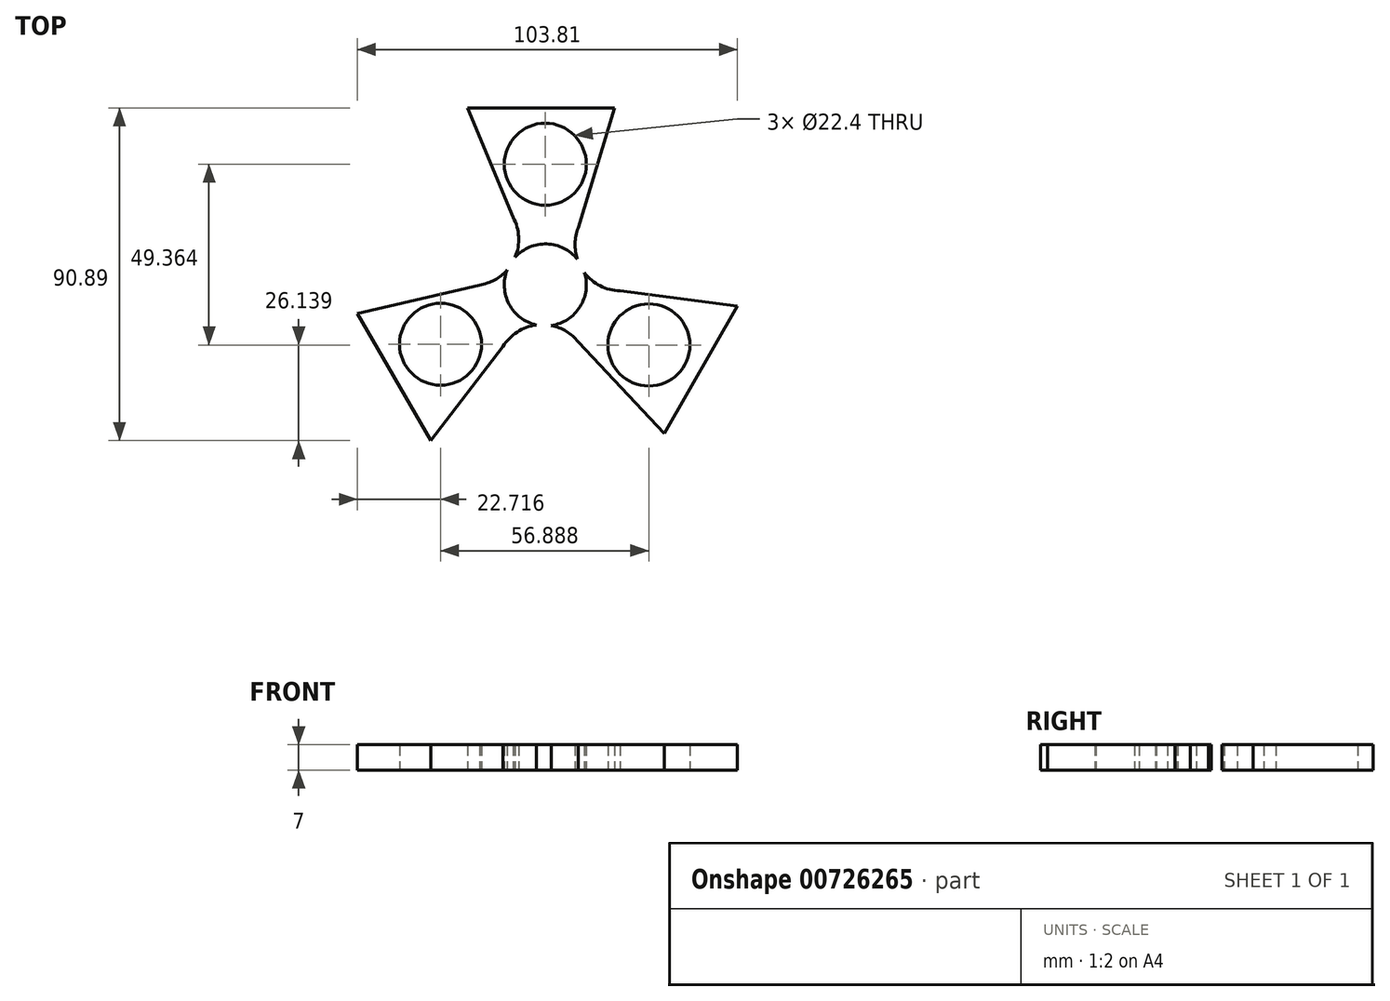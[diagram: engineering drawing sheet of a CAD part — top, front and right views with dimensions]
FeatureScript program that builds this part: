
annotation { "Feature Type Name" : "Feature", "Feature Type Description" : "" }
export const myFeature = defineFeature(function(context is Context, id is Id, definition is map)
    precondition{}
    {
        {
            var Q0;
            Q0=qCreatedBy(makeId("Top.planeOp"),FACE);
            var sketch = newSketch(context, id + "F0", { "sketchPlane" : qUnion([Q0])});
            skCircle(sketch, "E0", {"center": v(0, 0) * mm, "radius": 11.2 * mm});
            skCircle(sketch, "E1", {"center": v(0, 32.97) * mm, "radius": 11.2 * mm});
            skCircle(sketch, "E2.1.0", {"center": v(-28.61, -16.2) * mm, "radius": 11.2 * mm});
            skCircle(sketch, "E2.2.0", {"center": v(28.27, -16.4) * mm, "radius": 11.2 * mm});
            skPoint(sketch, "E2.center", {"position": v(-0.11, 0.13) * mm});
            skLineSegment(sketch, "E3", {"start": v(-5.26, 9.89) * mm, "end": v(-21.2, 48.36) * mm});
            skLineSegment(sketch, "E4", {"start": v(-21.2, 48.36) * mm, "end": v(18.9, 48.36) * mm});
            skLineSegment(sketch, "E5", {"start": v(18.9, 48.36) * mm, "end": v(6.94, 8.8) * mm});
            skLineSegment(sketch, "E6.1.0", {"start": v(-5.93, -9.5) * mm, "end": v(-31.28, -42.53) * mm});
            skLineSegment(sketch, "E6.1.1", {"start": v(-31.28, -42.53) * mm, "end": v(-51.33, -7.8) * mm});
            skLineSegment(sketch, "E6.1.2", {"start": v(-51.33, -7.8) * mm, "end": v(-11.08, 1.6) * mm});
            skLineSegment(sketch, "E6.2.0", {"start": v(11.2, -0.39) * mm, "end": v(52.48, -5.82) * mm});
            skLineSegment(sketch, "E6.2.1", {"start": v(52.48, -5.82) * mm, "end": v(32.42, -40.55) * mm});
            skLineSegment(sketch, "E6.2.2", {"start": v(32.42, -40.55) * mm, "end": v(4.15, -10.4) * mm});
            skArc(sketch, "E7", {"start": v(-17.96, 0) * mm, "mid": v(-8.57, 6.83) * mm, "end": v(-8.8, 18.45) * mm});
            skArc(sketch, "E8.1.0", {"start": v(8.98, -15.56) * mm, "mid": v(-1.63, -10.84) * mm, "end": v(-11.57, -16.85) * mm});
            skArc(sketch, "E8.2.0", {"start": v(8.98, 15.56) * mm, "mid": v(10.2, 4) * mm, "end": v(20.38, -1.6) * mm});
            skSolve(sketch);
        }
        {
            var Q0;
            Q0=makeQuery(id+"F0.imprint","IMPRINT",FACE,{"disambiguationData":[TD([[makeQuery(id+"F0.imprint","IMPRINT",EDGE,{"derivedFrom":sQuery(id+"F0.wireOp",EDGE,"E1")}),-1.0]])]});
            var Q1;
            Q1=makeQuery(id+"F0.imprint","IMPRINT",FACE,{"disambiguationData":[TD([[makeQuery(id+"F0.imprint","IMPRINT",EDGE,{"derivedFrom":sQuery(id+"F0.wireOp",EDGE,"E2.1.0")}),-1.0]])]});
            var Q2;
            Q2=makeQuery(id+"F0.imprint","IMPRINT",FACE,{"disambiguationData":[TD([[makeQuery(id+"F0.imprint","IMPRINT",EDGE,{"derivedFrom":sQuery(id+"F0.wireOp",EDGE,"E2.2.0")}),-1.0]])]});
            var Q3;
            {var subQ0=sQuery(id+"F0.wireOp",EDGE,"E3");var subQ1=sQuery(id+"F0.wireOp",EDGE,"E0");var subQ2=makeQuery(id+"F0.imprint","INTERSECT",VERTEX,{"derivedFrom":[subQ1,subQ0]});Q3=makeQuery(id+"F0.imprint","IMPRINT",FACE,{"disambiguationData":[TD([[makeQuery(id+"F0.imprint","IMPRINT",EDGE,{"disambiguationData":[TD([[subQ2,-1.0]])],"derivedFrom":subQ1}),-1.0]])]});}
            var Q4;
            {var subQ0=sQuery(id+"F0.wireOp",EDGE,"E6.2.0");var subQ1=sQuery(id+"F0.wireOp",EDGE,"E0");var subQ2=makeQuery(id+"F0.imprint","INTERSECT",VERTEX,{"derivedFrom":[subQ1,subQ0]});Q4=makeQuery(id+"F0.imprint","IMPRINT",FACE,{"disambiguationData":[TD([[makeQuery(id+"F0.imprint","IMPRINT",EDGE,{"disambiguationData":[TD([[subQ2,-1.0]])],"derivedFrom":subQ1}),-1.0]])]});}
            var Q5;
            {var subQ0=sQuery(id+"F0.wireOp",EDGE,"E5");var subQ1=sQuery(id+"F0.wireOp",EDGE,"E0");var subQ2=makeQuery(id+"F0.imprint","INTERSECT",VERTEX,{"derivedFrom":[subQ1,subQ0]});Q5=makeQuery(id+"F0.imprint","IMPRINT",FACE,{"disambiguationData":[TD([[makeQuery(id+"F0.imprint","IMPRINT",EDGE,{"disambiguationData":[TD([[subQ2,1.0]])],"derivedFrom":subQ1}),-1.0]])]});}
            var Q6;
            {var subQ0=sQuery(id+"F0.wireOp",EDGE,"E6.1.2");var subQ1=sQuery(id+"F0.wireOp",EDGE,"E0");var subQ2=makeQuery(id+"F0.imprint","INTERSECT",VERTEX,{"derivedFrom":[subQ1,subQ0]});Q6=makeQuery(id+"F0.imprint","IMPRINT",FACE,{"disambiguationData":[TD([[makeQuery(id+"F0.imprint","IMPRINT",EDGE,{"disambiguationData":[TD([[subQ2,1.0]])],"derivedFrom":subQ1}),-1.0]])]});}
            var Q7;
            {var subQ0=sQuery(id+"F0.wireOp",EDGE,"E6.1.0");var subQ1=sQuery(id+"F0.wireOp",EDGE,"E0");var subQ2=makeQuery(id+"F0.imprint","INTERSECT",VERTEX,{"derivedFrom":[subQ1,subQ0]});Q7=makeQuery(id+"F0.imprint","IMPRINT",FACE,{"disambiguationData":[TD([[makeQuery(id+"F0.imprint","IMPRINT",EDGE,{"disambiguationData":[TD([[subQ2,-1.0]])],"derivedFrom":subQ1}),-1.0]])]});}
            var Q8;
            {var subQ0=sQuery(id+"F0.wireOp",EDGE,"E6.2.2");var subQ1=sQuery(id+"F0.wireOp",EDGE,"E0");var subQ2=makeQuery(id+"F0.imprint","INTERSECT",VERTEX,{"derivedFrom":[subQ1,subQ0]});Q8=makeQuery(id+"F0.imprint","IMPRINT",FACE,{"disambiguationData":[TD([[makeQuery(id+"F0.imprint","IMPRINT",EDGE,{"disambiguationData":[TD([[subQ2,1.0]])],"derivedFrom":subQ1}),-1.0]])]});}
            extrude(context, id + "F1", {"entities" : qUnion([Q0, Q1, Q2, Q3, Q4, Q5, Q6, Q7, Q8]), "depth" : 7 * mm, "offsetDistance" : 25 * mm});
        }
    });
